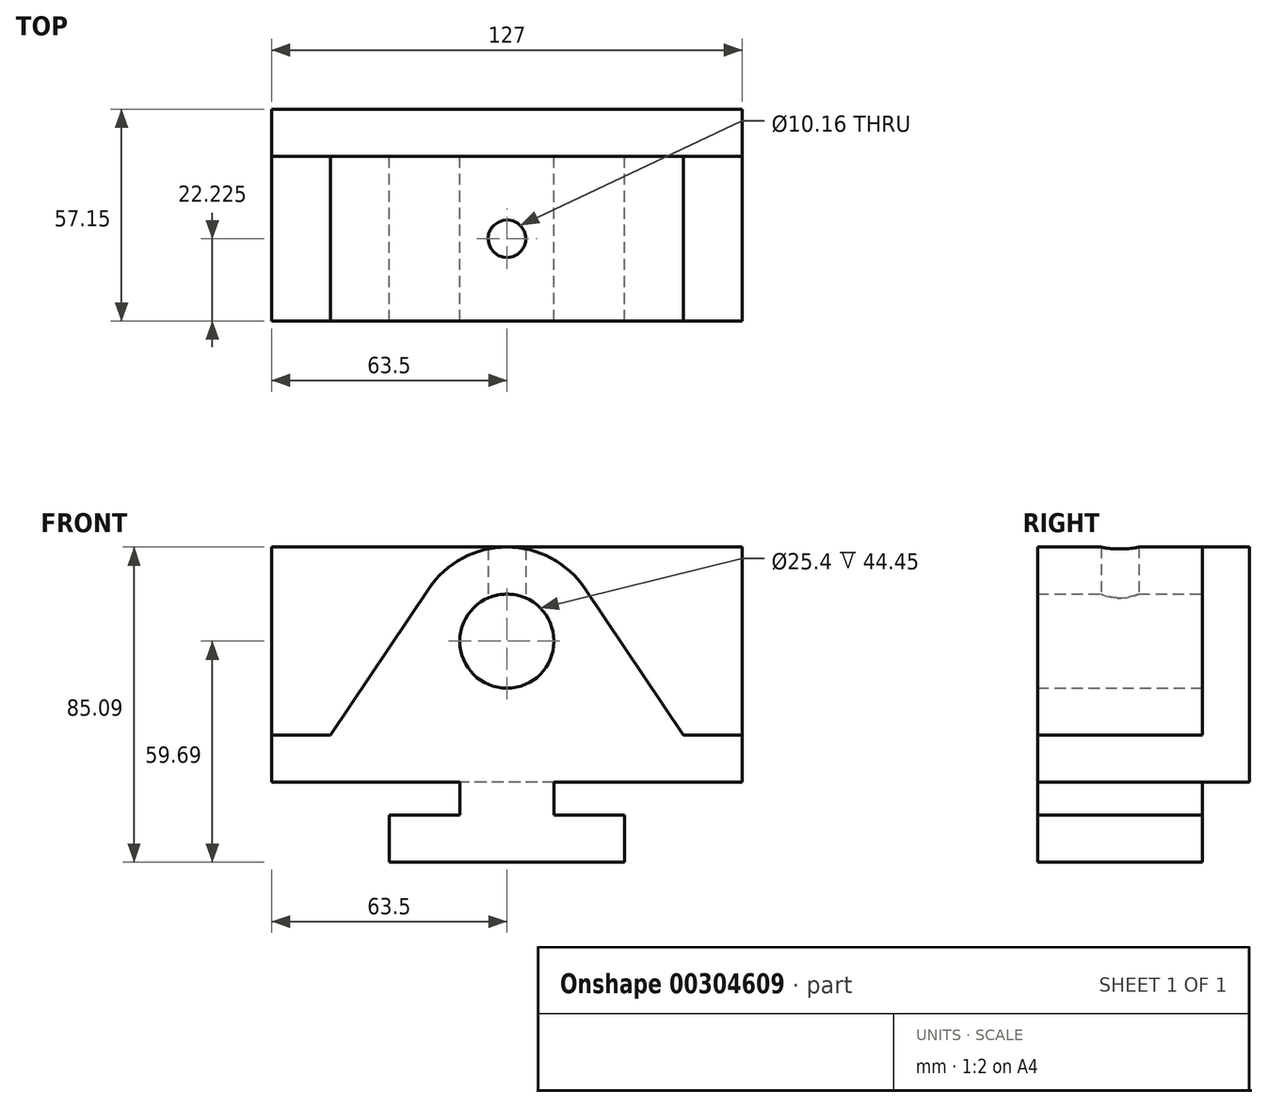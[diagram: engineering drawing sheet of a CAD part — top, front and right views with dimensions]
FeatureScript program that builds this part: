
annotation { "Feature Type Name" : "Feature", "Feature Type Description" : "" }
export const myFeature = defineFeature(function(context is Context, id is Id, definition is map)
    precondition{}
    {
        {
            var Q0;
            Q0=qCreatedBy(makeId("Front.planeOp"),FACE);
            var sketch = newSketch(context, id + "F0", { "sketchPlane" : qUnion([Q0])});
            skLineSegment(sketch, "E0", {"start": v(31.75, 0) * mm, "end": v(31.75, 12.7) * mm});
            skLineSegment(sketch, "E1", {"start": v(31.75, 12.7) * mm, "end": v(12.7, 12.7) * mm});
            skLineSegment(sketch, "E2", {"start": v(12.7, 12.7) * mm, "end": v(12.7, 21.6) * mm});
            skLineSegment(sketch, "E3", {"start": v(12.7, 21.6) * mm, "end": v(63.5, 21.6) * mm});
            skLineSegment(sketch, "E4", {"start": v(63.5, 21.6) * mm, "end": v(63.5, 34.3) * mm});
            skLineSegment(sketch, "E5", {"start": v(63.5, 34.3) * mm, "end": v(47.63, 34.3) * mm});
            skLineSegment(sketch, "E6", {"start": v(-31.75, 0) * mm, "end": v(-31.75, 12.7) * mm});
            skLineSegment(sketch, "E7", {"start": v(-31.75, 12.7) * mm, "end": v(-12.7, 12.7) * mm});
            skLineSegment(sketch, "E8", {"start": v(-12.7, 12.7) * mm, "end": v(-12.7, 21.6) * mm});
            skLineSegment(sketch, "E9", {"start": v(-12.7, 21.6) * mm, "end": v(-63.5, 21.6) * mm});
            skLineSegment(sketch, "E10", {"start": v(-63.5, 21.6) * mm, "end": v(-63.5, 34.3) * mm});
            skLineSegment(sketch, "E11", {"start": v(-63.5, 34.3) * mm, "end": v(-47.62, 34.3) * mm});
            skArc(sketch, "E12", {"start": v(21.1, 73.84) * mm, "mid": v(0, 85.1) * mm, "end": v(-21.1, 73.84) * mm});
            skCircle(sketch, "E13", {"center": v(0, 59.69) * mm, "radius": 12.7 * mm});
            skLineSegment(sketch, "E14", {"start": v(0, 0) * mm, "end": v(-31.75, 0) * mm});
            skLineSegment(sketch, "E15", {"start": v(31.75, 0) * mm, "end": v(0, 0) * mm});
            skLineSegment(sketch, "E16", {"start": v(-47.62, 34.3) * mm, "end": v(-21.1, 73.84) * mm});
            skLineSegment(sketch, "E17", {"start": v(21.1, 73.84) * mm, "end": v(47.63, 34.29) * mm});
            skSolve(sketch);
        }
        {
            var Q0;
            Q0 = qSketchRegion(id + "F0", true);
            extrude(context, id + "F1", {"entities" : qUnion([Q0]), "depth" : 44.45 * mm});
        }
        {
            var Q0;
            Q0=makeQuery(id+"F1.opExtrude","CAP_FACE",FACE,{"disambiguationData":[OSD([sQuery(id+"F0.wireOp",EDGE,"E0"),sQuery(id+"F0.wireOp",EDGE,"E1"),sQuery(id+"F0.wireOp",EDGE,"E2"),sQuery(id+"F0.wireOp",EDGE,"E3"),sQuery(id+"F0.wireOp",EDGE,"E4"),sQuery(id+"F0.wireOp",EDGE,"E5"),sQuery(id+"F0.wireOp",EDGE,"E6"),sQuery(id+"F0.wireOp",EDGE,"E7"),sQuery(id+"F0.wireOp",EDGE,"E8"),sQuery(id+"F0.wireOp",EDGE,"E9"),sQuery(id+"F0.wireOp",EDGE,"E10"),sQuery(id+"F0.wireOp",EDGE,"E11"),sQuery(id+"F0.wireOp",EDGE,"E12"),sQuery(id+"F0.wireOp",EDGE,"E13"),sQuery(id+"F0.wireOp",EDGE,"E14"),sQuery(id+"F0.wireOp",EDGE,"E15"),sQuery(id+"F0.wireOp",EDGE,"E16"),sQuery(id+"F0.wireOp",EDGE,"E17")])],"isStart":true});
            var sketch = newSketch(context, id + "F2", { "sketchPlane" : qUnion([Q0])});
            skLineSegment(sketch, "E18", {"start": v(0, 21.59) * mm, "end": v(63.5, 21.59) * mm});
            skLineSegment(sketch, "E19", {"start": v(63.5, 21.59) * mm, "end": v(63.5, 85.1) * mm});
            skLineSegment(sketch, "E20", {"start": v(63.5, 85.1) * mm, "end": v(-63.5, 85.1) * mm});
            skLineSegment(sketch, "E21", {"start": v(-63.5, 85.1) * mm, "end": v(-63.5, 21.6) * mm});
            skLineSegment(sketch, "E22", {"start": v(-63.5, 21.6) * mm, "end": v(0, 21.59) * mm});
            skSolve(sketch);
        }
        {
            var Q0;
            {var subQ0=makeQuery(id+"F1.opExtrude","CAP_EDGE",EDGE,{"disambiguationData":[OSD([sQuery(id+"F0.wireOp",EDGE,"E5")])],"isStart":true});Q0=makeQuery(id+"F2.imprint","IMPRINT",FACE,{"disambiguationData":[TD([[makeQuery(id+"F2.imprint","IMPRINT",EDGE,{"derivedFrom":subQ0}),1.0]])]});}
            var Q1;
            Q1 = qSketchRegion(id + "F2", true);
            extrude(context, id + "F3", {"entities" : qUnion([Q0, Q1]), "operationType" : NewBodyOperationType.ADD, "depth" : 12.7 * mm});
        }
        {
            var Q0;
            Q0=qCreatedBy(makeId("Top.planeOp"),FACE);
            var sketch = newSketch(context, id + "F4", { "sketchPlane" : qUnion([Q0])});
            skCircle(sketch, "E23", {"center": v(0, -22.23) * mm, "radius": 5.08 * mm});
            skSolve(sketch);
        }
        {
            var Q0;
            Q0 = qSketchRegion(id + "F4", true);
            extrude(context, id + "F5", {"entities" : qUnion([Q0]), "operationType" : NewBodyOperationType.REMOVE, "endBound" : BoundingType.THROUGH_ALL, "depth" : 25.4 * mm, "hasSecondDirection" : true, "secondDirectionOppositeDirection" : false, "secondDirectionDepth" : 63.5 * mm});
        }
    });
